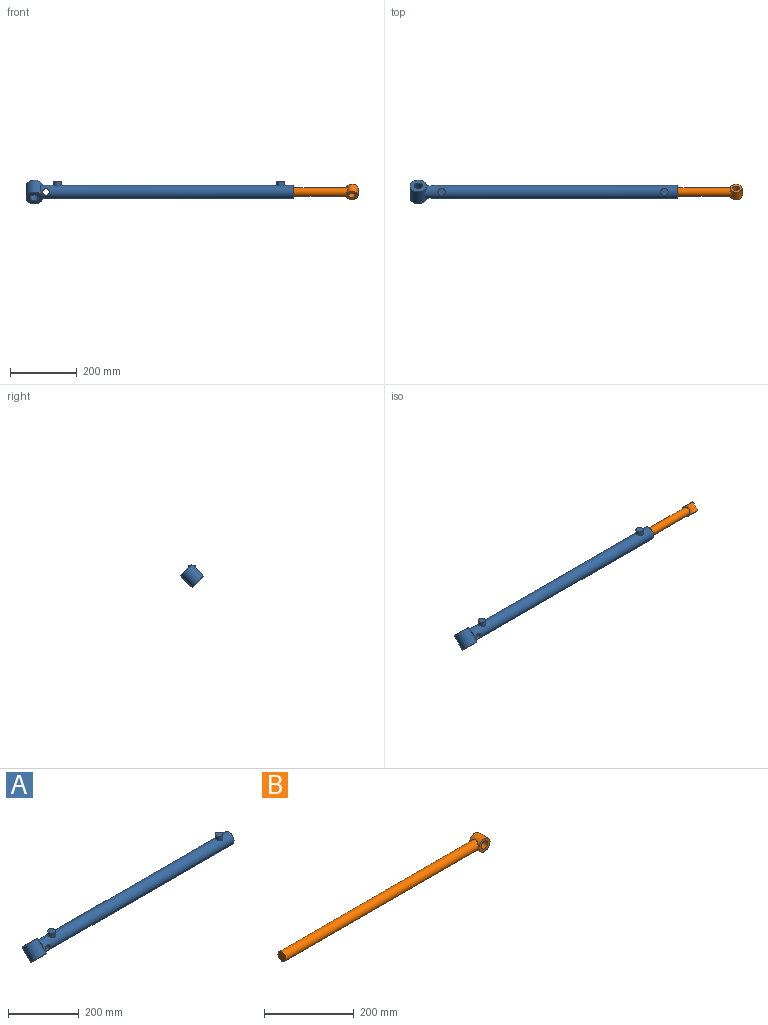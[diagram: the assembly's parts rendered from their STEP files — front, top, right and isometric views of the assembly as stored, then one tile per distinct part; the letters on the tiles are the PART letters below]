
ASSEMBLY  parts=2 mates=1
PART A: 18 faces, bbox 805x70.7x70.7 mm
  f0: cylinder r=20mm len=760mm, axis (-1,0,0), area 93843.3mm2, adj f1,f2,f4,f5,f7,f12,f14
  f1: plane 18.71x18.71mm, normal (-1,0,0), area 90.7mm2, adj f0,f14
  f2: plane 18.71x18.71mm, normal (-1,0,0), area 90.7mm2, adj f0,f14
  f3: cylinder r=12.5mm len=650mm, axis (1,0,0), area 50636.7mm2, adj f4,f6,f9,f10,f11
  f4: plane 40x40mm, normal (1,0,0), area 765.8mm2, adj f0,f3
  f5: cylinder r=10mm len=40mm, axis (0,-1,0), area 2348mm2, adj f0
  f6: plane 25x25mm, normal (1,0,0), area 490.9mm2, adj f3
  f7: cylinder r=11mm len=22mm, axis (0,0,-1), area 975.3mm2, adj f0,f8
  f8: plane 22x22mm, normal (0,0,1), area 380.1mm2, adj f7
  f9: plane 22x20mm, normal (0,0,-1), area 367.8mm2, adj f3,f10,f11
  f10: cylinder r=11mm len=20mm, axis (0,0,-1), area 79mm2, adj f3,f9
  f11: cylinder r=11mm len=20mm, axis (0,0,-1), area 79mm2, adj f3,f9
  f12: cylinder r=11mm len=22mm, axis (0,0,-1), area 975.3mm2, adj f0,f13
  f13: plane 22x22mm, normal (0,0,1), area 380.1mm2, adj f12
  f14: cylinder r=25mm len=70.71mm, axis (0,0.71,0.71), area 6709mm2, adj f0,f1,f2,f16,f17
  f15: cylinder r=12.5mm len=53.03mm, axis (0,0.71,0.71), area 3927mm2, adj f16,f17
  f16: plane 50x35.36mm, normal (0,-0.71,-0.71), area 1472.6mm2, adj f14,f15
  f17: plane 50x35.36mm, normal (0,0.71,0.71), area 1472.6mm2, adj f14,f15
PART B: 6 faces, bbox 642.5x30x35 mm
  f0: cylinder r=12.5mm len=612.75mm, axis (-1,0,0), area 47910.3mm2, adj f1,f2
  f1: plane 25x25mm, normal (-1,0,0), area 490.9mm2, adj f0
  f2: cylinder r=17.5mm len=35mm, axis (0,1,0), area 2768.2mm2, adj f0,f3,f4
  f3: plane 35x35mm, normal (0,-1,0), area 648mm2, adj f2,f5
  f4: plane 35x35mm, normal (0,1,0), area 648mm2, adj f2,f5
  f5: cylinder r=10mm len=30mm, axis (0,-1,0), area 1885mm2, adj f3,f4
PLACE A rot(axis=(-1,0,0),0deg) t=(1831.77,262.81,-242.16)mm
PLACE B rot(axis=(1,0,0),45deg) t=(1382.36,262.81,-242.16)mm
MATE slider B.f0 <-> A.f3  axis (-1,0,0) through (2142.36,262.81,-242.16)mm
